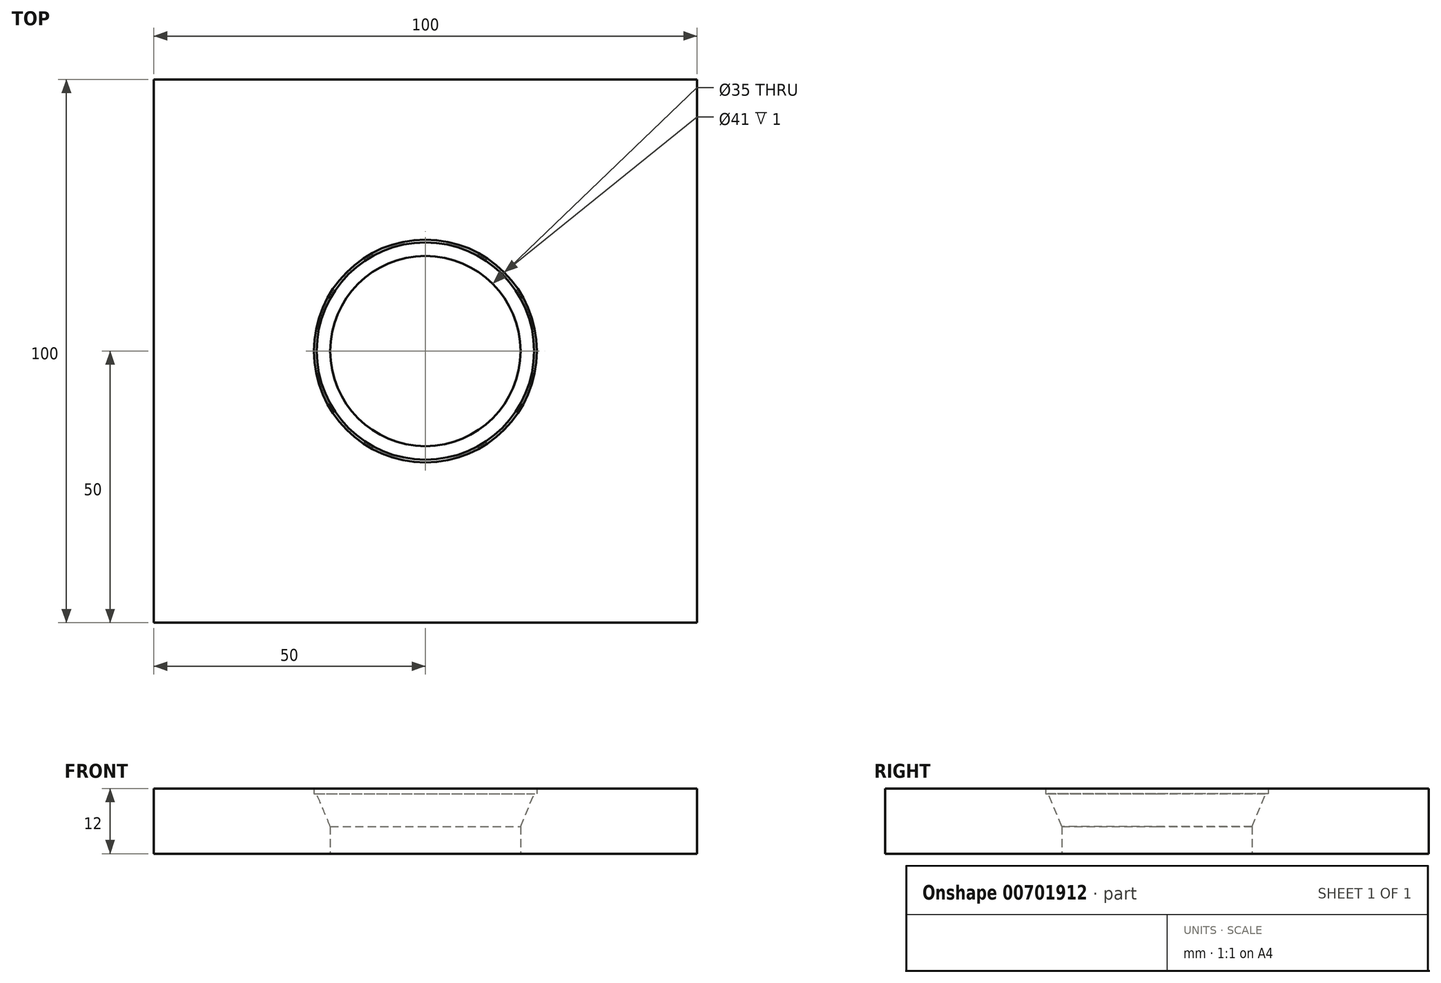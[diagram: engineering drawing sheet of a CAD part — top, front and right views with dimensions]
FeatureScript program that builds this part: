
annotation { "Feature Type Name" : "Feature", "Feature Type Description" : "" }
export const myFeature = defineFeature(function(context is Context, id is Id, definition is map)
    precondition{}
    {
        {
            var Q0;
            Q0=qCreatedBy(makeId("Front.planeOp"),FACE);
            var sketch = newSketch(context, id + "F0", { "sketchPlane" : qUnion([Q0])});
            skLineSegment(sketch, "E0", {"start": v(0, 0) * mm, "end": v(0, 50.74) * mm, "construction": true});
            skLineSegment(sketch, "E1", {"start": v(-17.5, 0) * mm, "end": v(-40, 0) * mm});
            skLineSegment(sketch, "E2", {"start": v(-40, 0) * mm, "end": v(-40, 12) * mm});
            skLineSegment(sketch, "E3", {"start": v(-40, 12) * mm, "end": v(-20.5, 12) * mm});
            skLineSegment(sketch, "E4", {"start": v(-20.5, 12) * mm, "end": v(-20.5, 11) * mm});
            skLineSegment(sketch, "E5", {"start": v(-20.5, 11) * mm, "end": v(-20, 11) * mm});
            skLineSegment(sketch, "E6", {"start": v(-17.5, 0) * mm, "end": v(-17.5, 5) * mm});
            skLineSegment(sketch, "E7", {"start": v(-17.5, 5) * mm, "end": v(-20, 11) * mm});
            skSolve(sketch);
        }
        {
            var Q0;
            Q0=makeQuery(id+"F0.imprint","IMPRINT",FACE,{"disambiguationData":[TD([[makeQuery(id+"F0.imprint","IMPRINT",EDGE,{"derivedFrom":sQuery(id+"F0.wireOp",EDGE,"E1")}),-1.0]])]});
            var Q1;
            Q1=sQuery(id+"F0.wireOp",EDGE,"E0");
            revolve(context, id + "F1", {"entities" : qUnion([Q0]), "axis" : qUnion([Q1]), "revolveType" : RevolveType.FULL, "surfaceOperationType" : NewSurfaceOperationType.NEW});
        }
        {
            var Q0;
            Q0=makeQuery(id+"F1.opRevolve","SWEPT_FACE",FACE,{"disambiguationData":[OSD([sQuery(id+"F0.wireOp",EDGE,"E3")])]});
            var sketch = newSketch(context, id + "F2", { "sketchPlane" : qUnion([Q0])});
            skLineSegment(sketch, "E8", {"start": v(-50, 50) * mm, "end": v(50, 50) * mm});
            skLineSegment(sketch, "E9", {"start": v(50, 50) * mm, "end": v(50, -50) * mm});
            skLineSegment(sketch, "E10", {"start": v(50, -50) * mm, "end": v(-50, -50) * mm});
            skLineSegment(sketch, "E11", {"start": v(-50, -50) * mm, "end": v(-50, 50) * mm});
            skSolve(sketch);
        }
        {
            var Q0;
            Q0=makeQuery(id+"F2.imprint","IMPRINT",FACE,{"disambiguationData":[TD([[makeQuery(id+"F2.imprint","IMPRINT",EDGE,{"derivedFrom":sQuery(id+"F2.wireOp",EDGE,"E8")}),-1.0]])]});
            var Q1;
            {var subQ0=sQuery(id+"F0.wireOp",EDGE,"E3");Q1=makeQuery(id+"F2.imprint","IMPRINT",FACE,{"disambiguationData":[TD([[makeQuery(id+"F2.imprint","IMPRINT",EDGE,{"derivedFrom":makeQuery(id+"F1.opRevolve","SWEPT_EDGE",EDGE,{"disambiguationData":[OSD([sQuery(id+"F0.wireOp",EDGE,"E2"),subQ0])]})}),-1.0]])]});}
            extrude(context, id + "F3", {"entities" : qUnion([Q0, Q1]), "operationType" : NewBodyOperationType.ADD, "oppositeDirection" : true, "depth" : 12 * mm, "offsetDistance" : 25 * mm});
        }
    });
